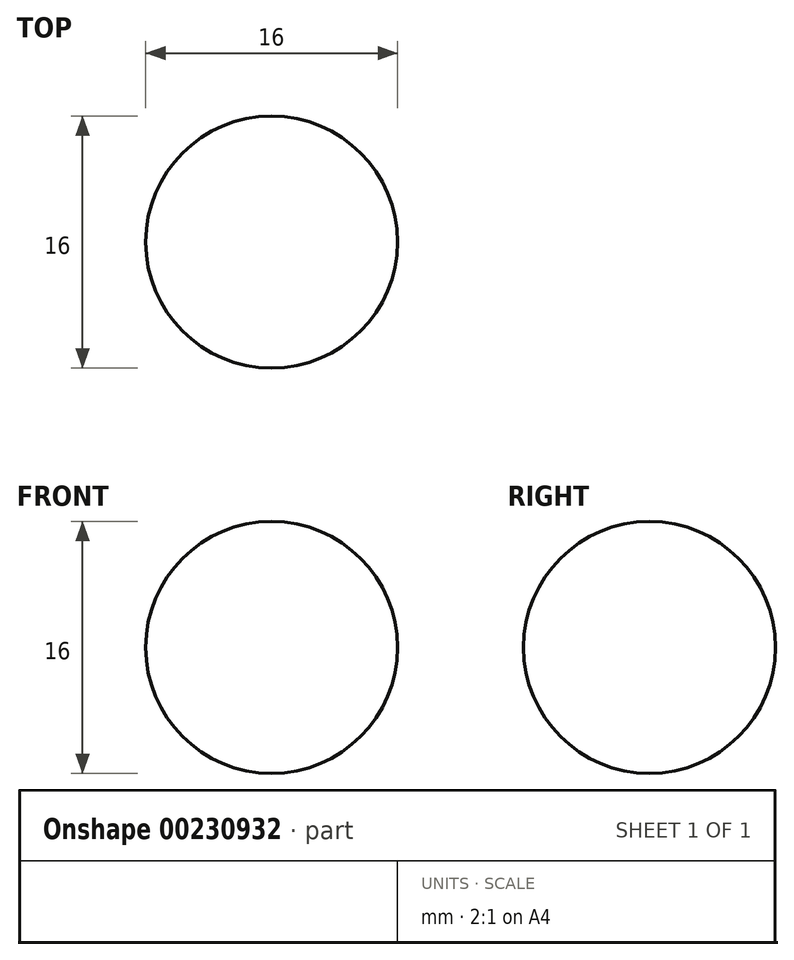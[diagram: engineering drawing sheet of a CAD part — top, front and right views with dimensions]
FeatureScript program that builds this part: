
annotation { "Feature Type Name" : "Feature", "Feature Type Description" : "" }
export const myFeature = defineFeature(function(context is Context, id is Id, definition is map)
    precondition{}
    {
        {
            var Q0;
            Q0=qCreatedBy(makeId("Front.planeOp"),FACE);
            var sketch = newSketch(context, id + "F0", { "sketchPlane" : qUnion([Q0])});
            skCircle(sketch, "E0", {"center": v(0, 0) * mm, "radius": 8 * mm});
            skLineSegment(sketch, "E1", {"start": v(0, 8) * mm, "end": v(0, -8) * mm});
            skSolve(sketch);
        }
        {
            var Q0;
            {var subQ0=sQuery(id+"F0.wireOp",EDGE,"E1");Q0=makeQuery(id+"F0.imprint","IMPRINT",FACE,{"disambiguationData":[TD([[makeQuery(id+"F0.imprint","IMPRINT",EDGE,{"derivedFrom":subQ0}),1.0]])]});}
            var Q1;
            Q1=sQuery(id+"F0.wireOp",EDGE,"E1");
            revolve(context, id + "F1", {"entities" : qUnion([Q0]), "axis" : qUnion([Q1]), "revolveType" : RevolveType.FULL});
        }
    });
